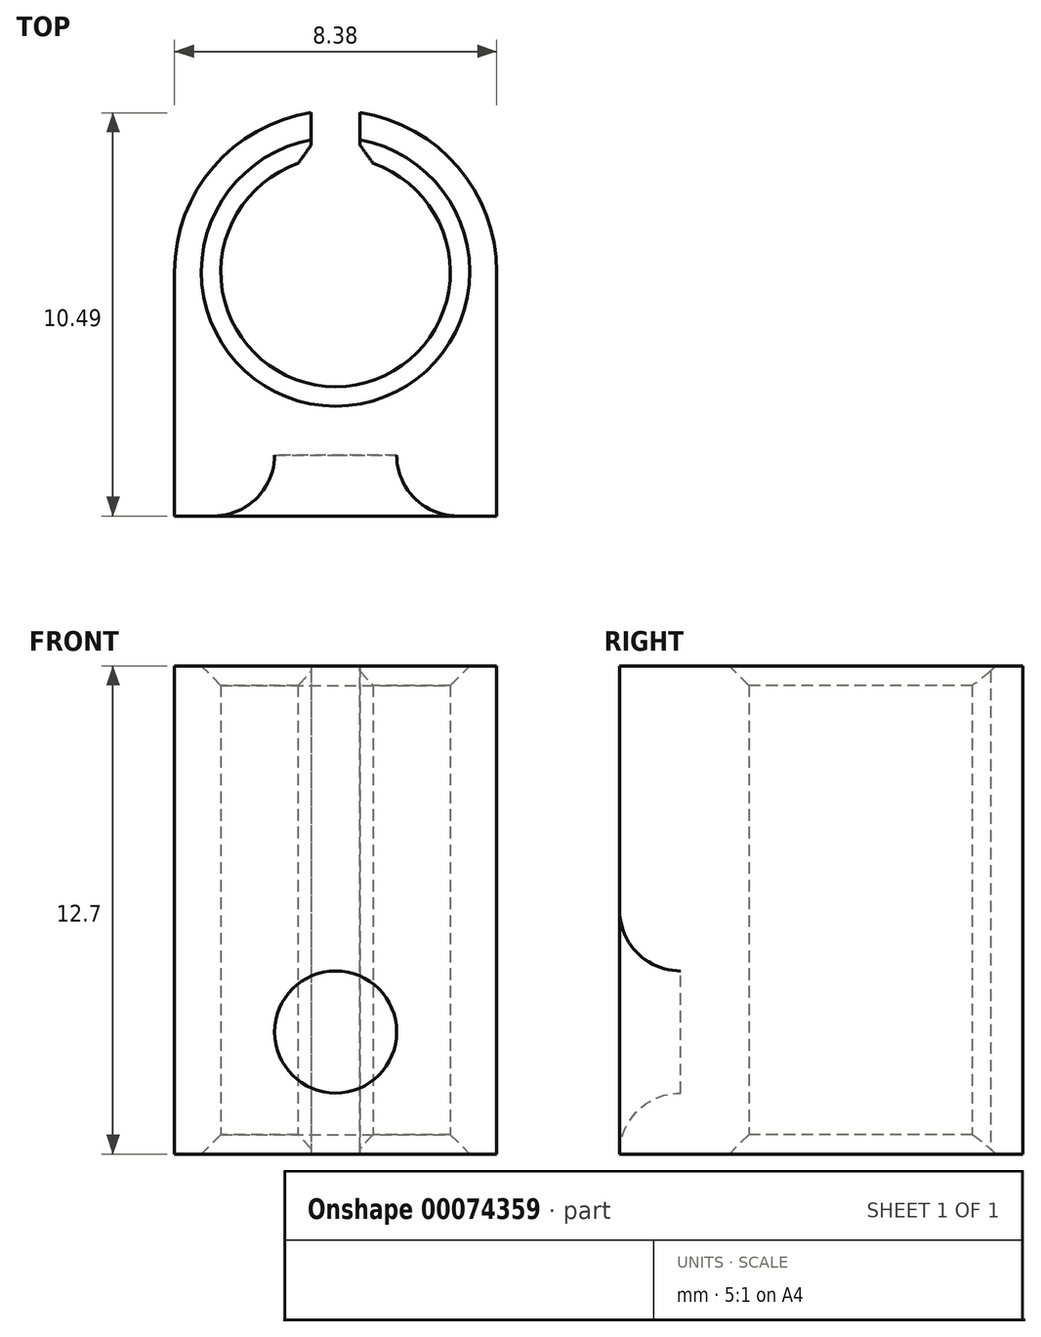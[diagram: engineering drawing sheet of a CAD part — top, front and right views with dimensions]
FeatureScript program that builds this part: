
annotation { "Feature Type Name" : "Feature", "Feature Type Description" : "" }
export const myFeature = defineFeature(function(context is Context, id is Id, definition is map)
    precondition{}
    {
        {
            var Q0;
            Q0=qCreatedBy(makeId("Top.planeOp"),FACE);
            var sketch = newSketch(context, id + "F0", { "sketchPlane" : qUnion([Q0])});
            skCircle(sketch, "E0", {"center": v(0, 0) * mm, "radius": 2.98 * mm});
            skCircle(sketch, "E1", {"center": v(0, 0) * mm, "radius": 4.2 * mm});
            skLineSegment(sketch, "E2", {"start": v(0, 0) * mm, "end": v(0, -4.2) * mm, "construction": true});
            skLineSegment(sketch, "E3", {"start": v(0, 0) * mm, "end": v(-0.64, 0) * mm});
            skLineSegment(sketch, "E4", {"start": v(-0.64, 0) * mm, "end": v(-0.64, 4.76) * mm});
            skLineSegment(sketch, "E5.MirrorCS", {"start": v(0, 0) * mm, "end": v(0.63, 0) * mm});
            skLineSegment(sketch, "E6.MirrorCS", {"start": v(0.63, 0) * mm, "end": v(0.63, 4.76) * mm});
            skLineSegment(sketch, "E7", {"start": v(-0.64, 4.76) * mm, "end": v(0.63, 4.76) * mm});
            skLineSegment(sketch, "E8", {"start": v(-4.2, 0) * mm, "end": v(-4.2, -4.76) * mm});
            skLineSegment(sketch, "E9", {"start": v(-4.2, -4.76) * mm, "end": v(0, -4.76) * mm});
            skLineSegment(sketch, "E10.MirrorCS", {"start": v(4.2, -4.76) * mm, "end": v(0, -4.76) * mm});
            skLineSegment(sketch, "E11.MirrorCS", {"start": v(4.2, 0) * mm, "end": v(4.2, -4.76) * mm});
            skSolve(sketch);
        }
        {
            var Q0;
            {var subQ3=sQuery(id+"F0.wireOp",EDGE,"E4");var subQ8=sQuery(id+"F0.wireOp",EDGE,"E0");var subQ9=makeQuery(id+"F0.imprint","INTERSECT",VERTEX,{"derivedFrom":[subQ8,subQ3]});Q0=makeQuery(id+"F0.imprint","IMPRINT",FACE,{"disambiguationData":[TD([[makeQuery(id+"F0.imprint","IMPRINT",EDGE,{"disambiguationData":[TD([[subQ9,-1.0]])],"derivedFrom":subQ8}),-1.0]])]});}
            var Q1;
            {var subQ2=sQuery(id+"F0.wireOp",EDGE,"e9759248-23e4-43c1-ad09-8139c4484e510.MirrorCS");Q1=makeQuery(id+"F0.imprint","IMPRINT",FACE,{"disambiguationData":[TD([[makeQuery(id+"F0.imprint","IMPRINT",EDGE,{"derivedFrom":subQ2}),-1.0]])]});}
            var Q2;
            {var subQ0=sQuery(id+"F0.wireOp",EDGE,"LeSR8eUU-es1b-GkyF-sqKM-tvtB5Nectiac");Q2=makeQuery(id+"F0.imprint","IMPRINT",FACE,{"disambiguationData":[TD([[makeQuery(id+"F0.imprint","IMPRINT",EDGE,{"derivedFrom":subQ0}),1.0]])]});}
            var Q3;
            {var subQ0=sQuery(id+"F0.wireOp",EDGE,"E8");Q3=makeQuery(id+"F0.imprint","IMPRINT",FACE,{"disambiguationData":[TD([[makeQuery(id+"F0.imprint","IMPRINT",EDGE,{"derivedFrom":subQ0}),1.0]])]});}
            extrude(context, id + "F1", {"entities" : qUnion([Q0, Q1, Q2, Q3]), "depth" : 12.7 * mm, "offsetDistance" : 25.4 * mm});
        }
        {
            var Q0;
            Q0=makeQuery(id+"F1.opExtrude","SWEPT_FACE",FACE,{"disambiguationData":[OSD([sQuery(id+"F0.wireOp",EDGE,"E9"),sQuery(id+"F0.wireOp",EDGE,"E10.MirrorCS")])]});
            var sketch = newSketch(context, id + "F2", { "sketchPlane" : qUnion([Q0])});
            skLineSegment(sketch, "E12", {"start": v(4.2, 6.35) * mm, "end": v(-4.2, 6.35) * mm, "construction": true});
            skCircle(sketch, "E13", {"center": v(0, 9.53) * mm, "radius": 1.59 * mm});
            skPoint(sketch, "E13.centerSnap0", {"position": v(0, 12.7) * mm});
            skCircle(sketch, "E14.MirrorC", {"center": v(0, 3.18) * mm, "radius": 1.59 * mm});
            skSolve(sketch);
        }
        {
            var Q0;
            Q0=makeQuery(id+"F2.imprint","IMPRINT",FACE,{"disambiguationData":[TD([[makeQuery(id+"F2.imprint","IMPRINT",EDGE,{"derivedFrom":sQuery(id+"F2.wireOp",EDGE,"E13")}),1.0]])]});
            var Q1;
            Q1=makeQuery(id+"F2.imprint","IMPRINT",FACE,{"disambiguationData":[TD([[makeQuery(id+"F2.imprint","IMPRINT",EDGE,{"derivedFrom":sQuery(id+"F2.wireOp",EDGE,"E14.MirrorC")}),-1.0]])]});
            extrude(context, id + "F3", {"entities" : qUnion([Q0, Q1]), "operationType" : NewBodyOperationType.ADD, "depth" : 1.59 * mm, "offsetDistance" : 25.4 * mm});
        }
        {
            var Q0;
            Q0=makeQuery(id+"F3.opExtrude","CAP_EDGE",EDGE,{"disambiguationData":[OSD([sQuery(id+"F2.wireOp",EDGE,"E13")])],"isStart":false});
            var Q1;
            Q1=makeQuery(id+"F3.opExtrude","CAP_EDGE",EDGE,{"disambiguationData":[OSD([sQuery(id+"F2.wireOp",EDGE,"E14.MirrorC")])],"isStart":false});
            fillet(context, id + "F4", {"entities" : qUnion([Q0, Q1]), "radius" : 1.59 * mm, "tangentPropagation" : true, "allowEdgeOverflow" : false});
        }
        {
            var Q0;
            Q0=makeQuery(id+"F1.opExtrude","SWEPT_FACE",FACE,{"disambiguationData":[OSD([sQuery(id+"F0.wireOp",EDGE,"E0")])]});
            chamfer(context, id + "F5", {"entities" : qUnion([Q0]), "width" : 0.5 * mm, "tangentPropagation" : true});
        }
    });
